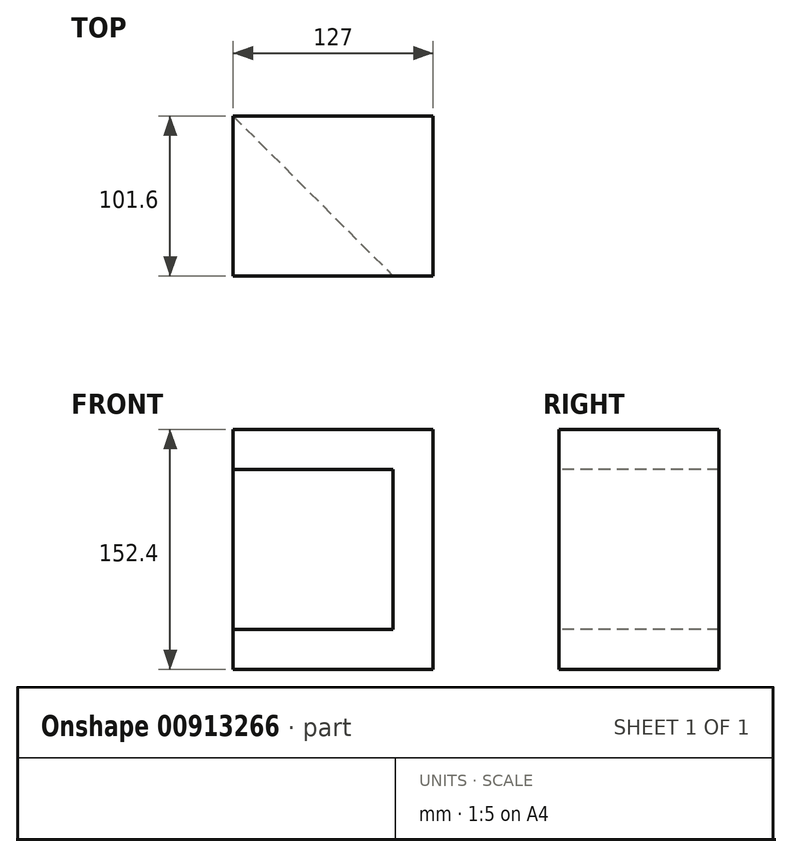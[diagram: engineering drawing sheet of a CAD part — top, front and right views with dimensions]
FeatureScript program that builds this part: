
annotation { "Feature Type Name" : "Feature", "Feature Type Description" : "" }
export const myFeature = defineFeature(function(context is Context, id is Id, definition is map)
    precondition{}
    {
        {
            var Q0;
            Q0=qCreatedBy(makeId("Top.planeOp"),FACE);
            var sketch = newSketch(context, id + "F0", { "sketchPlane" : qUnion([Q0])});
            skLineSegment(sketch, "E0.bottom", {"start": v(0, 0) * mm, "end": v(101.6, 0) * mm});
            skLineSegment(sketch, "E0.top", {"start": v(0, -101.6) * mm, "end": v(101.6, -101.6) * mm});
            skLineSegment(sketch, "E0.left", {"start": v(0, 0) * mm, "end": v(0, -101.6) * mm});
            skLineSegment(sketch, "E0.right", {"start": v(101.6, 0) * mm, "end": v(101.6, -101.6) * mm});
            skSolve(sketch);
        }
        {
            var Q0;
            Q0 = qSketchRegion(id + "F0", true);
            extrude(context, id + "F1", {"entities" : qUnion([Q0]), "depth" : 25.4 * mm, "offsetDistance" : 25.4 * mm});
        }
        {
            var Q0;
            Q0=makeQuery(id+"F1.opExtrude","CAP_FACE",FACE,{"disambiguationData":[OSD([sQuery(id+"F0.wireOp",EDGE,"E0.bottom"),sQuery(id+"F0.wireOp",EDGE,"E0.top"),sQuery(id+"F0.wireOp",EDGE,"E0.left"),sQuery(id+"F0.wireOp",EDGE,"E0.right")])],"isStart":false});
            var sketch = newSketch(context, id + "F2", { "sketchPlane" : qUnion([Q0])});
            skLineSegment(sketch, "E1.bottom", {"start": v(0, 0) * mm, "end": v(101.6, 0) * mm});
            skLineSegment(sketch, "E1.top", {"start": v(0, -101.6) * mm, "end": v(101.6, -101.6) * mm});
            skLineSegment(sketch, "E1.left", {"start": v(0, 0) * mm, "end": v(0, -101.6) * mm});
            skLineSegment(sketch, "E1.right", {"start": v(101.6, 0) * mm, "end": v(101.6, -101.6) * mm});
            skLineSegment(sketch, "E2", {"start": v(0, 0) * mm, "end": v(101.6, -101.6) * mm});
            skSolve(sketch);
        }
        {
            var Q0;
            Q0=makeQuery(id+"F2.imprint","IMPRINT",FACE,{"disambiguationData":[TD([[makeQuery(id+"F2.imprint","IMPRINT",EDGE,{"derivedFrom":sQuery(id+"F2.wireOp",EDGE,"E1.bottom")}),-1.0]])]});
            extrude(context, id + "F3", {"entities" : qUnion([Q0]), "operationType" : NewBodyOperationType.ADD, "depth" : 101.6 * mm, "offsetDistance" : 25.4 * mm});
        }
        {
            var Q0;
            Q0=makeQuery(id+"F3.opExtrude","CAP_FACE",FACE,{"disambiguationData":[OSD([sQuery(id+"F2.wireOp",EDGE,"E1.bottom"),sQuery(id+"F2.wireOp",EDGE,"E1.right"),sQuery(id+"F2.wireOp",EDGE,"E2")])],"isStart":false});
            var sketch = newSketch(context, id + "F4", { "sketchPlane" : qUnion([Q0])});
            skLineSegment(sketch, "E3.bottom", {"start": v(101.6, 0) * mm, "end": v(0, 0) * mm});
            skLineSegment(sketch, "E3.top", {"start": v(101.6, -101.6) * mm, "end": v(0, -101.6) * mm});
            skLineSegment(sketch, "E3.left", {"start": v(101.6, 0) * mm, "end": v(101.6, -101.6) * mm});
            skLineSegment(sketch, "E3.right", {"start": v(0, 0) * mm, "end": v(0, -101.6) * mm});
            skSolve(sketch);
        }
        {
            var Q0;
            Q0 = qSketchRegion(id + "F4", true);
            extrude(context, id + "F5", {"entities" : qUnion([Q0]), "operationType" : NewBodyOperationType.ADD, "depth" : 25.4 * mm, "offsetDistance" : 25.4 * mm});
        }
        {
            var Q0;
            Q0=makeQuery(id+"F5.boolean.opBoolean","MERGE",FACE,{"derivedFrom":[makeQuery(id+"F3.boolean.opBoolean","MERGE",FACE,{"derivedFrom":[makeQuery(id+"F1.opExtrude","SWEPT_FACE",FACE,{"disambiguationData":[OSD([sQuery(id+"F0.wireOp",EDGE,"E0.right")])]}),makeQuery(id+"F3.opExtrude","SWEPT_FACE",FACE,{"disambiguationData":[OSD([sQuery(id+"F2.wireOp",EDGE,"E1.right")])]})]}),makeQuery(id+"F5.opExtrude","SWEPT_FACE",FACE,{"disambiguationData":[OSD([sQuery(id+"F4.wireOp",EDGE,"E3.left")])]})]});
            extrude(context, id + "F6", {"entities" : qUnion([Q0]), "operationType" : NewBodyOperationType.ADD, "depth" : 25.4 * mm, "offsetDistance" : 25.4 * mm});
        }
    });
